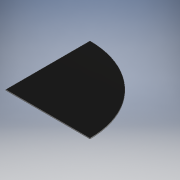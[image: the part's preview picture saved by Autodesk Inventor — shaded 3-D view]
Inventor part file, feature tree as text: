
AUTODESK INVENTOR PART (.ipt)
format: ipt  version: 2016 (Build 200138000, 138)  size: 107,008 bytes
history: native  units: mm
features: extrude x1, sketch x1
ambient origin geometry x8: Origin, YZ Plane, XZ Plane, XY Plane, X Axis, Y Axis, Z Axis, Center Point
bodies: 实体1 (feature_tree)
feature tree (2):
  extrude  "拉伸1"  Depth=500.0mm
  sketch  "草图1"  dims[d0=500.0mm d1=500.0mm d2=90.0deg d3=500.0mm d4=5.0mm d5=0.0mm]
